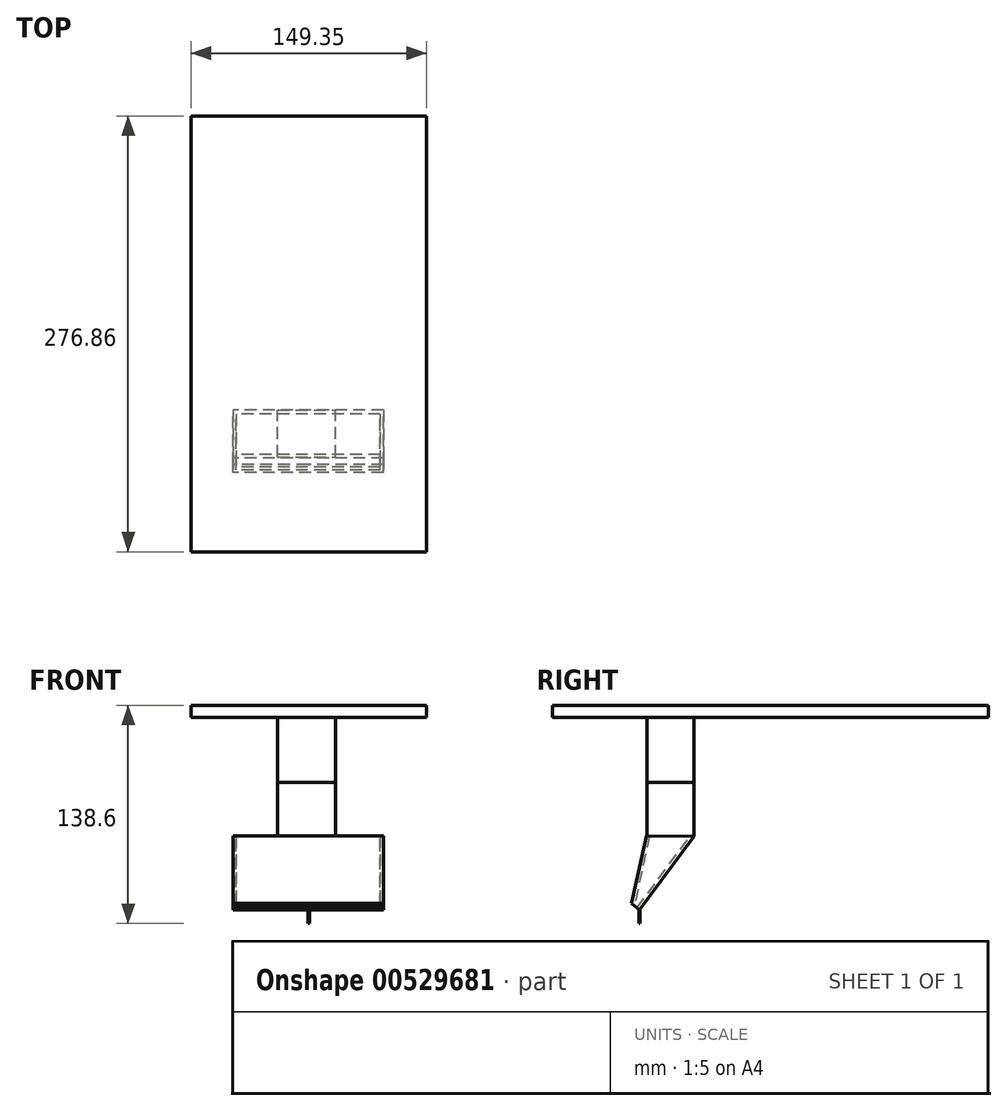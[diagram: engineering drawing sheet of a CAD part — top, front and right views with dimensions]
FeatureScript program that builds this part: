
annotation { "Feature Type Name" : "Feature", "Feature Type Description" : "" }
export const myFeature = defineFeature(function(context is Context, id is Id, definition is map)
    precondition{}
    {
        {
            var Q0;
            Q0=qCreatedBy(makeId("Front.planeOp"),FACE);
            var sketch = newSketch(context, id + "F0", { "sketchPlane" : qUnion([Q0])});
            skLineSegment(sketch, "E0.bottom", {"start": v(-74.3, 73.53) * mm, "end": v(75.06, 73.53) * mm});
            skLineSegment(sketch, "E0.top", {"start": v(-74.3, 65.91) * mm, "end": v(75.06, 65.91) * mm});
            skLineSegment(sketch, "E0.left", {"start": v(-74.3, 73.53) * mm, "end": v(-74.3, 65.91) * mm});
            skLineSegment(sketch, "E0.right", {"start": v(75.06, 73.53) * mm, "end": v(75.06, 65.91) * mm});
            skSolve(sketch);
        }
        {
            var Q0;
            Q0 = qSketchRegion(id + "F0", true);
            extrude(context, id + "F1", {"entities" : qUnion([Q0]), "endBound" : BoundingType.SYMMETRIC, "depth" : 276.86 * mm, "offsetDistance" : 25.4 * mm});
        }
        {
            var Q0;
            Q0=makeQuery(id+"F1.opExtrude","SWEPT_FACE",FACE,{"disambiguationData":[OSD([sQuery(id+"F0.wireOp",EDGE,"E0.top")])]});
            var sketch = newSketch(context, id + "F2", { "sketchPlane" : qUnion([Q0])});
            skLineSegment(sketch, "E1.bottom", {"start": v(-19.38, 78.21) * mm, "end": v(17.3, 78.21) * mm});
            skLineSegment(sketch, "E1.top", {"start": v(-19.38, 48.45) * mm, "end": v(17.3, 48.45) * mm});
            skLineSegment(sketch, "E1.left", {"start": v(-19.38, 78.21) * mm, "end": v(-19.38, 48.45) * mm});
            skLineSegment(sketch, "E1.right", {"start": v(17.3, 78.21) * mm, "end": v(17.3, 48.45) * mm});
            skSolve(sketch);
        }
        {
            var Q0;
            Q0 = qSketchRegion(id + "F2", true);
            extrude(context, id + "F3", {"entities" : qUnion([Q0]), "operationType" : NewBodyOperationType.ADD, "depth" : 41.4 * mm, "offsetDistance" : 25.4 * mm});
        }
        {
            var Q0;
            Q0=makeQuery(id+"F3.opExtrude","CAP_FACE",FACE,{"disambiguationData":[OSD([sQuery(id+"F2.wireOp",EDGE,"E1.bottom"),sQuery(id+"F2.wireOp",EDGE,"E1.top"),sQuery(id+"F2.wireOp",EDGE,"E1.left"),sQuery(id+"F2.wireOp",EDGE,"E1.right")])],"isStart":false});
            var sketch = newSketch(context, id + "F4", { "sketchPlane" : qUnion([Q0])});
            skLineSegment(sketch, "E2.bottom", {"start": v(-19.38, 78.21) * mm, "end": v(17.3, 78.21) * mm});
            skLineSegment(sketch, "E2.top", {"start": v(-19.38, 48.45) * mm, "end": v(17.3, 48.45) * mm});
            skLineSegment(sketch, "E2.left", {"start": v(-19.38, 78.21) * mm, "end": v(-19.38, 48.45) * mm});
            skLineSegment(sketch, "E2.right", {"start": v(17.3, 78.21) * mm, "end": v(17.3, 48.45) * mm});
            skSolve(sketch);
        }
        {
            var Q0;
            Q0=makeQuery(id+"F4.imprint","IMPRINT",FACE,{"disambiguationData":[TD([[makeQuery(id+"F4.imprint","IMPRINT",EDGE,{"derivedFrom":sQuery(id+"F4.wireOp",EDGE,"E2.bottom")}),-1.0]])]});
            extrude(context, id + "F5", {"entities" : qUnion([Q0]), "depth" : 34.3 * mm, "offsetDistance" : 25.4 * mm});
        }
        {
            var Q0;
            Q0=qCreatedBy(makeId("Right.planeOp"),FACE);
            var sketch = newSketch(context, id + "F6", { "sketchPlane" : qUnion([Q0])});
            skLineSegment(sketch, "E3", {"start": v(-78.76, -9.52) * mm, "end": v(-88.2, -52.32) * mm});
            skLineSegment(sketch, "E4", {"start": v(-88.2, -52.32) * mm, "end": v(-82.93, -56.3) * mm});
            skLineSegment(sketch, "E5", {"start": v(-82.93, -56.3) * mm, "end": v(-48.41, -9.64) * mm});
            skLineSegment(sketch, "E6", {"start": v(-48.41, -9.64) * mm, "end": v(-78.76, -9.52) * mm});
            skSolve(sketch);
        }
        {
            var Q0;
            Q0 = qSketchRegion(id + "F6", true);
            extrude(context, id + "F7", {"entities" : qUnion([Q0]), "endBound" : BoundingType.SYMMETRIC, "depth" : 95.5 * mm, "offsetDistance" : 25.4 * mm});
        }
        {
            var Q0;
            Q0=makeQuery(id+"F7.opExtrude","SWEPT_FACE",FACE,{"disambiguationData":[OSD([sQuery(id+"F6.wireOp",EDGE,"E4")])]});
            var Q1;
            Q1=makeQuery(id+"F7.opExtrude","SWEPT_FACE",FACE,{"disambiguationData":[OSD([sQuery(id+"F6.wireOp",EDGE,"E6")])]});
            shell(context, id + "F8", {"entities" : qUnion([Q0, Q1]), "thickness" : 2.03 * mm});
        }
        {
            var Q0;
            Q0=qCreatedBy(makeId("Right.planeOp"),FACE);
            var sketch = newSketch(context, id + "F9", { "sketchPlane" : qUnion([Q0])});
            skLineSegment(sketch, "E7.bottom", {"start": v(-83.24, -56.04) * mm, "end": v(-82.83, -56.04) * mm});
            skLineSegment(sketch, "E7.top", {"start": v(-83.24, -65.07) * mm, "end": v(-82.83, -65.07) * mm});
            skLineSegment(sketch, "E7.left", {"start": v(-83.24, -56.04) * mm, "end": v(-83.24, -65.07) * mm});
            skLineSegment(sketch, "E7.right", {"start": v(-82.83, -56.04) * mm, "end": v(-82.83, -65.07) * mm});
            skSolve(sketch);
        }
        {
            var Q0;
            Q0 = qSketchRegion(id + "F9", true);
            extrude(context, id + "F10", {"entities" : qUnion([Q0]), "operationType" : NewBodyOperationType.ADD, "depth" : 1.02 * mm, "offsetDistance" : 25.4 * mm});
        }
    });
